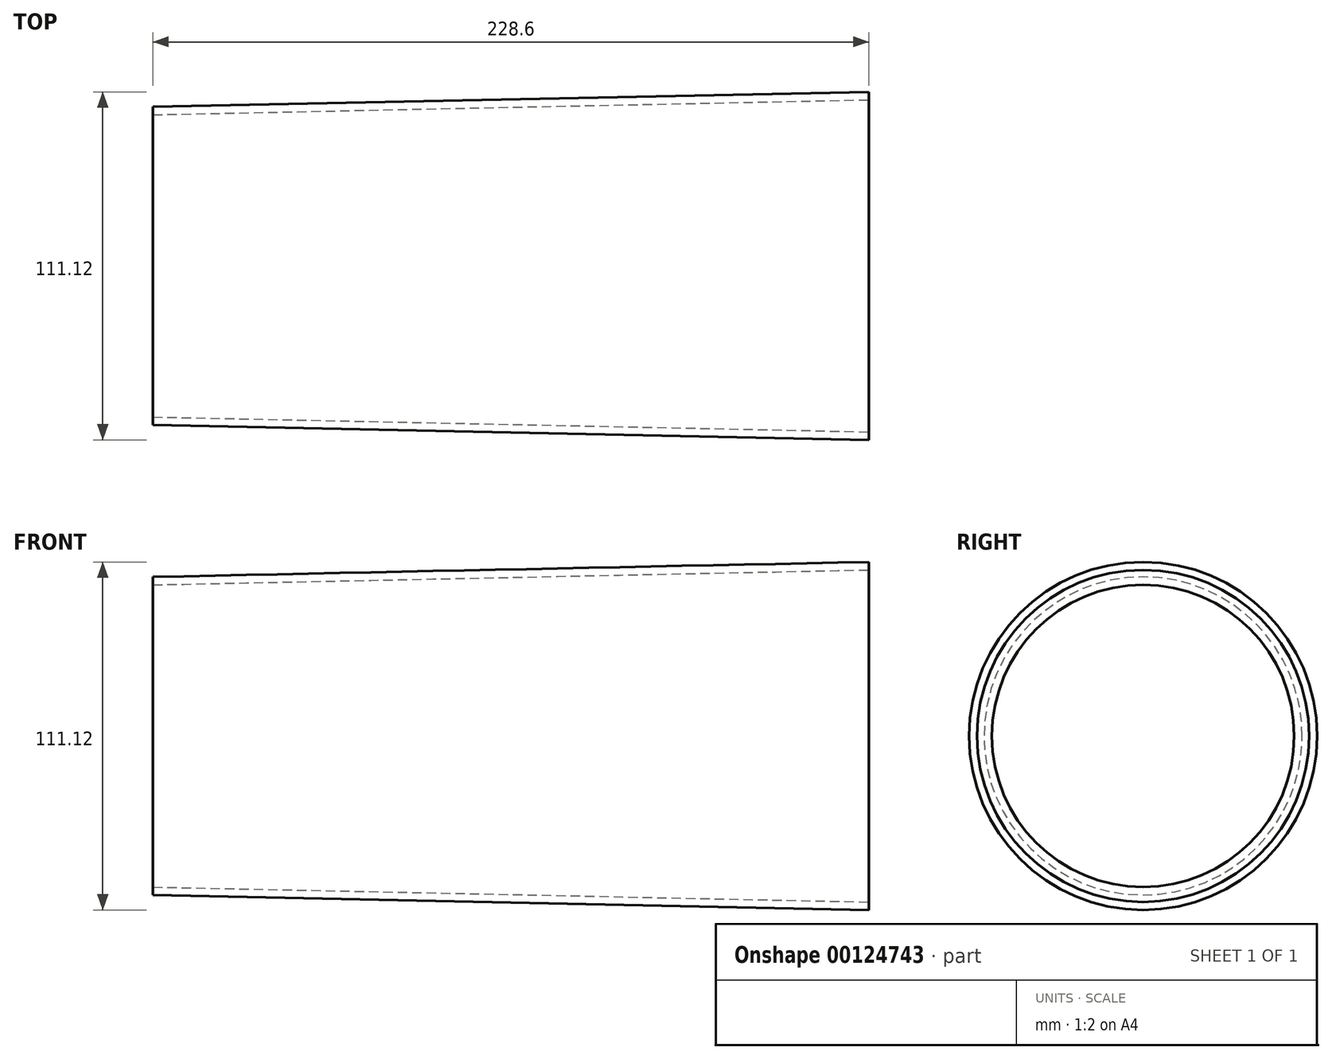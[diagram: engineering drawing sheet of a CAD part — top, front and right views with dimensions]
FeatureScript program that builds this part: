
annotation { "Feature Type Name" : "Feature", "Feature Type Description" : "" }
export const myFeature = defineFeature(function(context is Context, id is Id, definition is map)
    precondition{}
    {
        {
            var Q0;
            Q0=qCreatedBy(makeId("Top.planeOp"),FACE);
            var sketch = newSketch(context, id + "F0", { "sketchPlane" : qUnion([Q0])});
            skLineSegment(sketch, "E0", {"start": v(-138.35, -10.22) * mm, "end": v(90.25, -10.22) * mm});
            skLineSegment(sketch, "E1", {"start": v(-138.35, -10.22) * mm, "end": v(-138.35, 40.58) * mm});
            skLineSegment(sketch, "E2", {"start": v(90.25, -10.22) * mm, "end": v(90.25, 45.34) * mm});
            skLineSegment(sketch, "E3", {"start": v(-138.35, 40.58) * mm, "end": v(90.25, 45.34) * mm});
            skSolve(sketch);
        }
        {
            var Q0;
            Q0=makeQuery(id+"F0.imprint","IMPRINT",FACE,{"disambiguationData":[TD([[makeQuery(id+"F0.imprint","IMPRINT",EDGE,{"derivedFrom":sQuery(id+"F0.wireOp",EDGE,"E0")}),1.0]])]});
            var Q1;
            Q1=sQuery(id+"F0.wireOp",EDGE,"E0");
            var Q2;
            Q2=sQuery(id+"F0.wireOp",EDGE,"E0");
            revolve(context, id + "F1", {"entities" : qUnion([Q0]), "surfaceEntities" : qUnion([Q1]), "axis" : qUnion([Q2]), "revolveType" : RevolveType.FULL});
        }
        {
            var Q0;
            Q0=makeQuery(id+"F1.opRevolve","SWEPT_FACE",FACE,{"disambiguationData":[OSD([sQuery(id+"F0.wireOp",EDGE,"E2")])]});
            var Q1;
            Q1=makeQuery(id+"F1.opRevolve","SWEPT_FACE",FACE,{"disambiguationData":[OSD([sQuery(id+"F0.wireOp",EDGE,"E1")])]});
            shell(context, id + "F2", {"entities" : qUnion([Q0, Q1]), "thickness" : 2.54 * mm});
        }
    });
